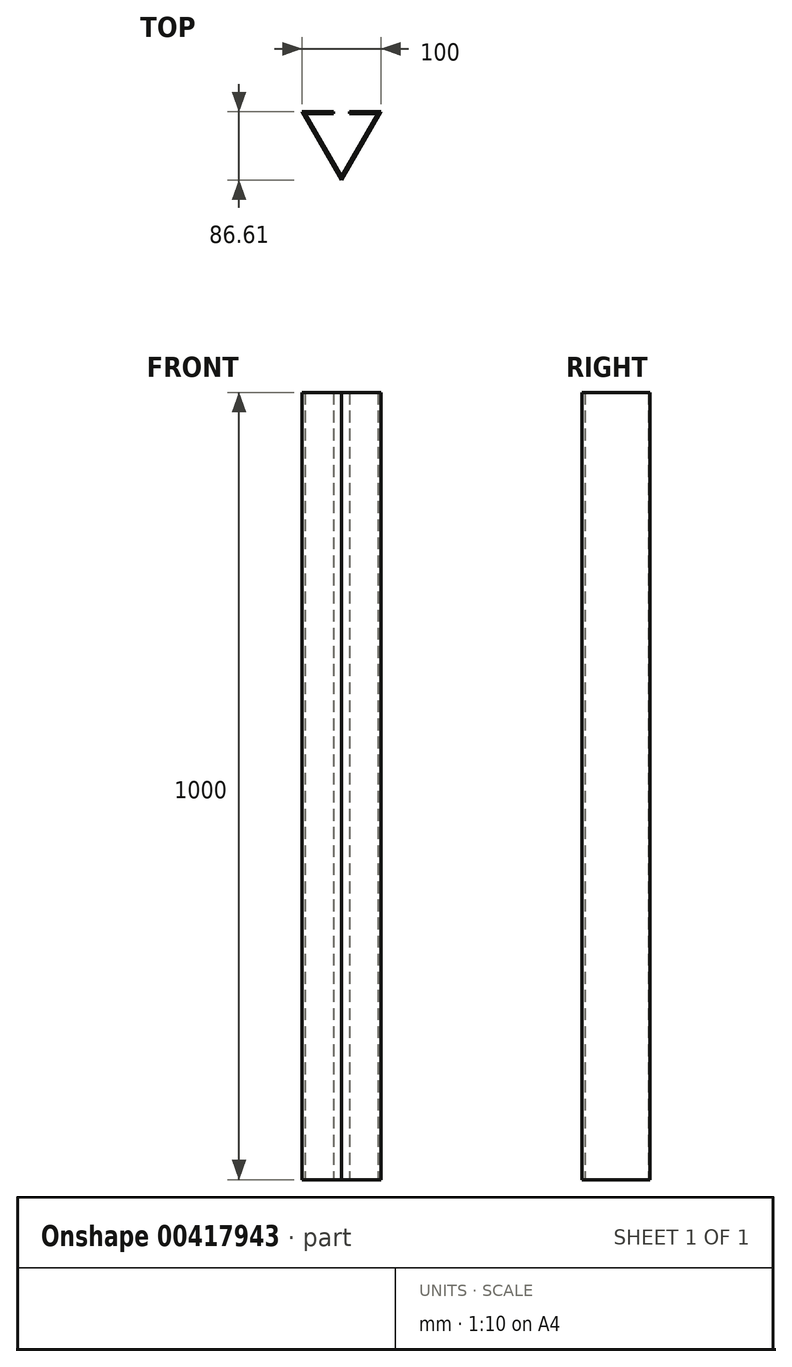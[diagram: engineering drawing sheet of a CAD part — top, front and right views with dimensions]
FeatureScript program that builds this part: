
annotation { "Feature Type Name" : "Feature", "Feature Type Description" : "" }
export const myFeature = defineFeature(function(context is Context, id is Id, definition is map)
    precondition{}
    {
        {
            var Q0;
            Q0=qCreatedBy(makeId("Top.planeOp"),FACE);
            var sketch = newSketch(context, id + "F0", { "sketchPlane" : qUnion([Q0])});
            skCircle(sketch, "E0.cCircle", {"center": v(0, 0) * mm, "radius": 57.74 * mm, "construction": true});
            skLineSegment(sketch, "E0.0", {"start": v(0, -57.74) * mm, "end": v(-50, 28.87) * mm});
            skLineSegment(sketch, "E0.1", {"start": v(-50, 28.87) * mm, "end": v(-10, 28.87) * mm});
            skLineSegment(sketch, "E0.2", {"start": v(50, 28.87) * mm, "end": v(0, -57.74) * mm});
            skLineSegment(sketch, "E1", {"start": v(10, 28.87) * mm, "end": v(50, 28.87) * mm});
            skLineSegment(sketch, "E2.0", {"start": v(-46.54, 26.87) * mm, "end": v(-10, 26.87) * mm});
            skLineSegment(sketch, "E2.1", {"start": v(0, -53.74) * mm, "end": v(-46.54, 26.87) * mm});
            skLineSegment(sketch, "E2.2", {"start": v(46.54, 26.87) * mm, "end": v(0, -53.74) * mm});
            skLineSegment(sketch, "E2.3", {"start": v(10, 26.87) * mm, "end": v(46.54, 26.87) * mm});
            skLineSegment(sketch, "E3", {"start": v(-10, 28.87) * mm, "end": v(-10, 26.87) * mm});
            skLineSegment(sketch, "E4", {"start": v(10, 28.87) * mm, "end": v(10, 26.87) * mm});
            skSolve(sketch);
        }
        {
            var Q0;
            Q0=makeQuery(id+"F0.imprint","IMPRINT",FACE,{"disambiguationData":[TD([[makeQuery(id+"F0.imprint","IMPRINT",EDGE,{"derivedFrom":sQuery(id+"F0.wireOp",EDGE,"E0.0")}),-1.0]])]});
            extrude(context, id + "F1", {"entities" : qUnion([Q0]), "depth" : 1000 * mm, "offsetDistance" : 25 * mm});
        }
    });
